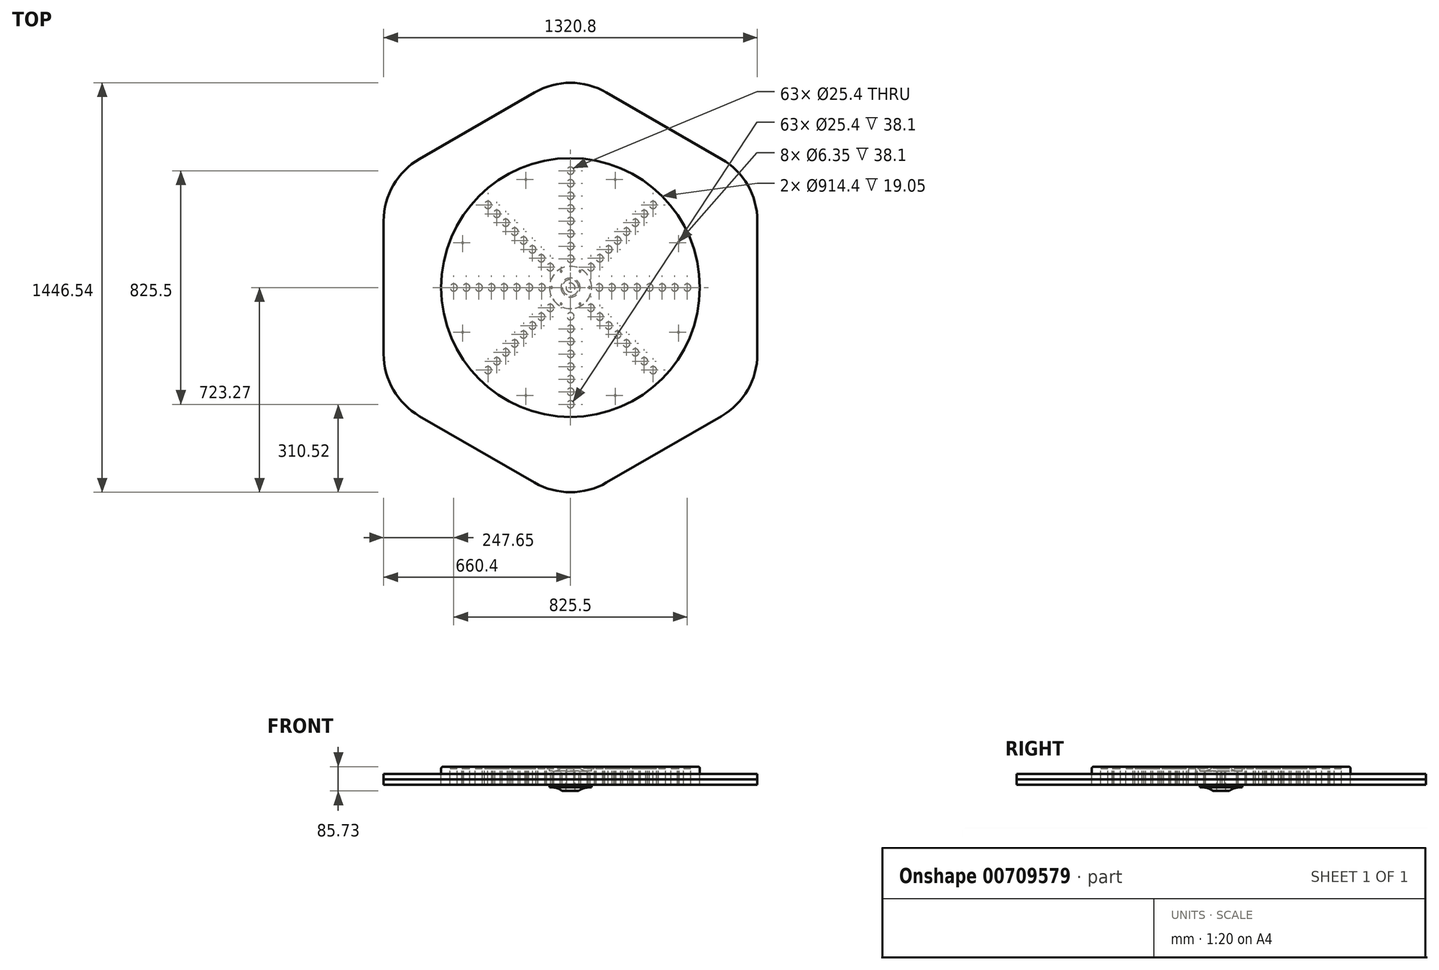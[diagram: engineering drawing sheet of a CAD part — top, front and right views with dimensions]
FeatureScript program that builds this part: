
annotation { "Feature Type Name" : "Feature", "Feature Type Description" : "" }
export const myFeature = defineFeature(function(context is Context, id is Id, definition is map)
    precondition{}
    {
        {
            var Q0;
            Q0=qCreatedBy(makeId("Top.planeOp"),FACE);
            var sketch = newSketch(context, id + "F0", { "sketchPlane" : qUnion([Q0])});
            skCircle(sketch, "E0", {"center": v(0, 0) * mm, "radius": 457.2 * mm});
            skSolve(sketch);
        }
        {
            var Q0;
            Q0=makeQuery(id+"F0.imprint","IMPRINT",FACE,{"disambiguationData":[TD([[makeQuery(id+"F0.imprint","IMPRINT",EDGE,{"derivedFrom":sQuery(id+"F0.wireOp",EDGE,"E0")}),1.0]])]});
            extrude(context, id + "F1", {"entities" : qUnion([Q0]), "oppositeDirection" : true, "depth" : 6.35 * mm, "offsetDistance" : 25.4 * mm});
        }
        {
            var Q0;
            Q0=makeQuery(id+"F1.opExtrude","CAP_FACE",FACE,{"disambiguationData":[OSD([sQuery(id+"F0.wireOp",EDGE,"E0")])],"isStart":false});
            var sketch = newSketch(context, id + "F2", { "sketchPlane" : qUnion([Q0])});
            skCircle(sketch, "E1", {"center": v(0, 0) * mm, "radius": 457.2 * mm});
            skLineSegment(sketch, "E2", {"start": v(0, 0) * mm, "end": v(457.2, 0) * mm, "construction": true});
            skCircle(sketch, "E3", {"center": v(101.6, 0) * mm, "radius": 12.7 * mm});
            skCircle(sketch, "E4.1.0.0", {"center": v(146.05, 0) * mm, "radius": 12.7 * mm});
            skCircle(sketch, "E4.2.0.0", {"center": v(190.5, 0) * mm, "radius": 12.7 * mm});
            skCircle(sketch, "E4.3.0.0", {"center": v(234.95, 0) * mm, "radius": 12.7 * mm});
            skCircle(sketch, "E4.4.0.0", {"center": v(279.4, 0) * mm, "radius": 12.7 * mm});
            skCircle(sketch, "E4.5.0.0", {"center": v(323.85, 0) * mm, "radius": 12.7 * mm});
            skCircle(sketch, "E4.6.0.0", {"center": v(368.3, 0) * mm, "radius": 12.7 * mm});
            skCircle(sketch, "E4.7.0.0", {"center": v(412.75, 0) * mm, "radius": 12.7 * mm});
            skLineSegment(sketch, "E4.direction1", {"start": v(101.6, 0) * mm, "end": v(146.05, 0) * mm, "construction": true});
            skCircle(sketch, "E5.1.0", {"center": v(103.27, 103.27) * mm, "radius": 12.7 * mm});
            skCircle(sketch, "E5.1.1", {"center": v(229, 229) * mm, "radius": 12.7 * mm});
            skCircle(sketch, "E5.1.2", {"center": v(71.84, 71.84) * mm, "radius": 12.7 * mm});
            skCircle(sketch, "E5.1.3", {"center": v(260.43, 260.43) * mm, "radius": 12.7 * mm});
            skCircle(sketch, "E5.1.4", {"center": v(291.86, 291.86) * mm, "radius": 12.7 * mm});
            skCircle(sketch, "E5.1.5", {"center": v(134.7, 134.7) * mm, "radius": 12.7 * mm});
            skCircle(sketch, "E5.1.6", {"center": v(166.13, 166.13) * mm, "radius": 12.7 * mm});
            skLineSegment(sketch, "E5.1.7", {"start": v(71.84, 71.84) * mm, "end": v(103.27, 103.27) * mm, "construction": true});
            skCircle(sketch, "E5.1.8", {"center": v(197.57, 197.57) * mm, "radius": 12.7 * mm});
            skCircle(sketch, "E5.2.0", {"center": v(0, 146.05) * mm, "radius": 12.7 * mm});
            skCircle(sketch, "E5.2.1", {"center": v(0, 323.85) * mm, "radius": 12.7 * mm});
            skCircle(sketch, "E5.2.2", {"center": v(0, 101.6) * mm, "radius": 12.7 * mm});
            skCircle(sketch, "E5.2.3", {"center": v(0, 368.3) * mm, "radius": 12.7 * mm});
            skCircle(sketch, "E5.2.4", {"center": v(0, 412.75) * mm, "radius": 12.7 * mm});
            skCircle(sketch, "E5.2.5", {"center": v(0, 190.5) * mm, "radius": 12.7 * mm});
            skCircle(sketch, "E5.2.6", {"center": v(0, 234.95) * mm, "radius": 12.7 * mm});
            skLineSegment(sketch, "E5.2.7", {"start": v(0, 101.6) * mm, "end": v(0, 146.05) * mm, "construction": true});
            skCircle(sketch, "E5.2.8", {"center": v(0, 279.4) * mm, "radius": 12.7 * mm});
            skCircle(sketch, "E5.3.0", {"center": v(-103.27, 103.27) * mm, "radius": 12.7 * mm});
            skCircle(sketch, "E5.3.1", {"center": v(-229, 229) * mm, "radius": 12.7 * mm});
            skCircle(sketch, "E5.3.2", {"center": v(-71.84, 71.84) * mm, "radius": 12.7 * mm});
            skCircle(sketch, "E5.3.3", {"center": v(-260.43, 260.43) * mm, "radius": 12.7 * mm});
            skCircle(sketch, "E5.3.4", {"center": v(-291.86, 291.86) * mm, "radius": 12.7 * mm});
            skCircle(sketch, "E5.3.5", {"center": v(-134.7, 134.7) * mm, "radius": 12.7 * mm});
            skCircle(sketch, "E5.3.6", {"center": v(-166.13, 166.13) * mm, "radius": 12.7 * mm});
            skLineSegment(sketch, "E5.3.7", {"start": v(-71.84, 71.84) * mm, "end": v(-103.27, 103.27) * mm, "construction": true});
            skCircle(sketch, "E5.3.8", {"center": v(-197.57, 197.57) * mm, "radius": 12.7 * mm});
            skCircle(sketch, "E5.4.0", {"center": v(-146.05, 0) * mm, "radius": 12.7 * mm});
            skCircle(sketch, "E5.4.1", {"center": v(-323.85, 0) * mm, "radius": 12.7 * mm});
            skCircle(sketch, "E5.4.2", {"center": v(-101.6, 0) * mm, "radius": 12.7 * mm});
            skCircle(sketch, "E5.4.3", {"center": v(-368.3, 0) * mm, "radius": 12.7 * mm});
            skCircle(sketch, "E5.4.4", {"center": v(-412.75, 0) * mm, "radius": 12.7 * mm});
            skCircle(sketch, "E5.4.5", {"center": v(-190.5, 0) * mm, "radius": 12.7 * mm});
            skCircle(sketch, "E5.4.6", {"center": v(-234.95, 0) * mm, "radius": 12.7 * mm});
            skLineSegment(sketch, "E5.4.7", {"start": v(-101.6, 0) * mm, "end": v(-146.05, 0) * mm, "construction": true});
            skCircle(sketch, "E5.4.8", {"center": v(-279.4, 0) * mm, "radius": 12.7 * mm});
            skCircle(sketch, "E5.5.0", {"center": v(-103.27, -103.27) * mm, "radius": 12.7 * mm});
            skCircle(sketch, "E5.5.1", {"center": v(-229, -229) * mm, "radius": 12.7 * mm});
            skCircle(sketch, "E5.5.2", {"center": v(-71.84, -71.84) * mm, "radius": 12.7 * mm});
            skCircle(sketch, "E5.5.3", {"center": v(-260.43, -260.43) * mm, "radius": 12.7 * mm});
            skCircle(sketch, "E5.5.4", {"center": v(-291.86, -291.86) * mm, "radius": 12.7 * mm});
            skCircle(sketch, "E5.5.5", {"center": v(-134.7, -134.7) * mm, "radius": 12.7 * mm});
            skCircle(sketch, "E5.5.6", {"center": v(-166.13, -166.13) * mm, "radius": 12.7 * mm});
            skLineSegment(sketch, "E5.5.7", {"start": v(-71.84, -71.84) * mm, "end": v(-103.27, -103.27) * mm, "construction": true});
            skCircle(sketch, "E5.5.8", {"center": v(-197.57, -197.57) * mm, "radius": 12.7 * mm});
            skCircle(sketch, "E5.6.0", {"center": v(0, -146.05) * mm, "radius": 12.7 * mm});
            skCircle(sketch, "E5.6.1", {"center": v(0, -323.85) * mm, "radius": 12.7 * mm});
            skCircle(sketch, "E5.6.2", {"center": v(0, -101.6) * mm, "radius": 12.7 * mm});
            skCircle(sketch, "E5.6.3", {"center": v(0, -368.3) * mm, "radius": 12.7 * mm});
            skCircle(sketch, "E5.6.4", {"center": v(0, -412.75) * mm, "radius": 12.7 * mm});
            skCircle(sketch, "E5.6.5", {"center": v(0, -190.5) * mm, "radius": 12.7 * mm});
            skCircle(sketch, "E5.6.6", {"center": v(0, -234.95) * mm, "radius": 12.7 * mm});
            skLineSegment(sketch, "E5.6.7", {"start": v(0, -101.6) * mm, "end": v(0, -146.05) * mm, "construction": true});
            skCircle(sketch, "E5.6.8", {"center": v(0, -279.4) * mm, "radius": 12.7 * mm});
            skCircle(sketch, "E5.7.0", {"center": v(103.27, -103.27) * mm, "radius": 12.7 * mm});
            skCircle(sketch, "E5.7.1", {"center": v(229, -229) * mm, "radius": 12.7 * mm});
            skCircle(sketch, "E5.7.2", {"center": v(71.84, -71.84) * mm, "radius": 12.7 * mm});
            skCircle(sketch, "E5.7.3", {"center": v(260.43, -260.43) * mm, "radius": 12.7 * mm});
            skCircle(sketch, "E5.7.4", {"center": v(291.86, -291.86) * mm, "radius": 12.7 * mm});
            skCircle(sketch, "E5.7.5", {"center": v(134.7, -134.7) * mm, "radius": 12.7 * mm});
            skCircle(sketch, "E5.7.6", {"center": v(166.13, -166.13) * mm, "radius": 12.7 * mm});
            skLineSegment(sketch, "E5.7.7", {"start": v(71.84, -71.84) * mm, "end": v(103.27, -103.27) * mm, "construction": true});
            skCircle(sketch, "E5.7.8", {"center": v(197.57, -197.57) * mm, "radius": 12.7 * mm});
            skLineSegment(sketch, "E6", {"start": v(0, -412.75) * mm, "end": v(0, 0) * mm, "construction": true});
            skLineSegment(sketch, "E7", {"start": v(0, 0) * mm, "end": v(291.86, -704.6) * mm, "construction": true});
            skCircle(sketch, "E8", {"center": v(0, 0) * mm, "radius": 412.75 * mm, "construction": true});
            skPoint(sketch, "E9", {"position": v(157.95, -381.33) * mm});
            skCircle(sketch, "E10", {"center": v(157.95, -381.33) * mm, "radius": 3.18 * mm});
            skPoint(sketch, "E11.1.0", {"position": v(381.33, -157.95) * mm});
            skPoint(sketch, "E11.2.0", {"position": v(381.33, 157.95) * mm});
            skPoint(sketch, "E11.3.0", {"position": v(157.95, 381.33) * mm});
            skPoint(sketch, "E11.4.0", {"position": v(-157.95, 381.33) * mm});
            skPoint(sketch, "E11.5.0", {"position": v(-381.33, 157.95) * mm});
            skPoint(sketch, "E11.6.0", {"position": v(-381.33, -157.95) * mm});
            skPoint(sketch, "E11.7.0", {"position": v(-157.95, -381.33) * mm});
            skCircle(sketch, "E12", {"center": v(0, 0) * mm, "radius": 74.61 * mm});
            skCircle(sketch, "E13.1.0", {"center": v(381.33, -157.95) * mm, "radius": 3.18 * mm});
            skCircle(sketch, "E13.2.0", {"center": v(381.33, 157.95) * mm, "radius": 3.18 * mm});
            skCircle(sketch, "E13.3.0", {"center": v(157.95, 381.33) * mm, "radius": 3.18 * mm});
            skCircle(sketch, "E13.4.0", {"center": v(-157.95, 381.33) * mm, "radius": 3.18 * mm});
            skCircle(sketch, "E13.5.0", {"center": v(-381.33, 157.95) * mm, "radius": 3.18 * mm});
            skCircle(sketch, "E13.6.0", {"center": v(-381.33, -157.95) * mm, "radius": 3.18 * mm});
            skCircle(sketch, "E13.7.0", {"center": v(-157.95, -381.33) * mm, "radius": 3.18 * mm});
            skSolve(sketch);
        }
        {
            var Q0;
            Q0=makeQuery(id+"F2.imprint","IMPRINT",FACE,{"disambiguationData":[TD([[makeQuery(id+"F2.imprint","IMPRINT",EDGE,{"derivedFrom":sQuery(id+"F2.wireOp",EDGE,"E1")}),-1.0]])]});
            extrude(context, id + "F3", {"entities" : qUnion([Q0]), "depth" : 19.05 * mm, "offsetDistance" : 25.4 * mm});
        }
        {
            var Q0;
            Q0=makeQuery(id+"F3.opExtrude","CAP_FACE",FACE,{"disambiguationData":[OSD([sQuery(id+"F2.wireOp",EDGE,"E1"),sQuery(id+"F2.wireOp",EDGE,"E3"),sQuery(id+"F2.wireOp",EDGE,"E4.1.0.0"),sQuery(id+"F2.wireOp",EDGE,"E4.2.0.0"),sQuery(id+"F2.wireOp",EDGE,"E4.3.0.0"),sQuery(id+"F2.wireOp",EDGE,"E4.4.0.0"),sQuery(id+"F2.wireOp",EDGE,"E4.5.0.0"),sQuery(id+"F2.wireOp",EDGE,"E4.6.0.0"),sQuery(id+"F2.wireOp",EDGE,"E4.7.0.0"),sQuery(id+"F2.wireOp",EDGE,"E5.1.0"),sQuery(id+"F2.wireOp",EDGE,"E5.1.1"),sQuery(id+"F2.wireOp",EDGE,"E5.1.2"),sQuery(id+"F2.wireOp",EDGE,"E5.1.3"),sQuery(id+"F2.wireOp",EDGE,"E5.1.4"),sQuery(id+"F2.wireOp",EDGE,"E5.1.5"),sQuery(id+"F2.wireOp",EDGE,"E5.1.6"),sQuery(id+"F2.wireOp",EDGE,"E5.1.8"),sQuery(id+"F2.wireOp",EDGE,"E5.2.0"),sQuery(id+"F2.wireOp",EDGE,"E5.2.1"),sQuery(id+"F2.wireOp",EDGE,"E5.2.2"),sQuery(id+"F2.wireOp",EDGE,"E5.2.3"),sQuery(id+"F2.wireOp",EDGE,"E5.2.4"),sQuery(id+"F2.wireOp",EDGE,"E5.2.5"),sQuery(id+"F2.wireOp",EDGE,"E5.2.6"),sQuery(id+"F2.wireOp",EDGE,"E5.2.8"),sQuery(id+"F2.wireOp",EDGE,"E5.3.0"),sQuery(id+"F2.wireOp",EDGE,"E5.3.1"),sQuery(id+"F2.wireOp",EDGE,"E5.3.2"),sQuery(id+"F2.wireOp",EDGE,"E5.3.3"),sQuery(id+"F2.wireOp",EDGE,"E5.3.4"),sQuery(id+"F2.wireOp",EDGE,"E5.3.5"),sQuery(id+"F2.wireOp",EDGE,"E5.3.6"),sQuery(id+"F2.wireOp",EDGE,"E5.3.8"),sQuery(id+"F2.wireOp",EDGE,"E5.4.0"),sQuery(id+"F2.wireOp",EDGE,"E5.4.1"),sQuery(id+"F2.wireOp",EDGE,"E5.4.2"),sQuery(id+"F2.wireOp",EDGE,"E5.4.3"),sQuery(id+"F2.wireOp",EDGE,"E5.4.4"),sQuery(id+"F2.wireOp",EDGE,"E5.4.5"),sQuery(id+"F2.wireOp",EDGE,"E5.4.6"),sQuery(id+"F2.wireOp",EDGE,"E5.4.8"),sQuery(id+"F2.wireOp",EDGE,"E5.5.0"),sQuery(id+"F2.wireOp",EDGE,"E5.5.1"),sQuery(id+"F2.wireOp",EDGE,"E5.5.2"),sQuery(id+"F2.wireOp",EDGE,"E5.5.3"),sQuery(id+"F2.wireOp",EDGE,"E5.5.4"),sQuery(id+"F2.wireOp",EDGE,"E5.5.5"),sQuery(id+"F2.wireOp",EDGE,"E5.5.6"),sQuery(id+"F2.wireOp",EDGE,"E5.5.8"),sQuery(id+"F2.wireOp",EDGE,"E5.6.0"),sQuery(id+"F2.wireOp",EDGE,"E5.6.1"),sQuery(id+"F2.wireOp",EDGE,"E5.6.2"),sQuery(id+"F2.wireOp",EDGE,"E5.6.3"),sQuery(id+"F2.wireOp",EDGE,"E5.6.4"),sQuery(id+"F2.wireOp",EDGE,"E5.6.5"),sQuery(id+"F2.wireOp",EDGE,"E5.6.6"),sQuery(id+"F2.wireOp",EDGE,"E5.6.8"),sQuery(id+"F2.wireOp",EDGE,"E5.7.0"),sQuery(id+"F2.wireOp",EDGE,"E5.7.1"),sQuery(id+"F2.wireOp",EDGE,"E5.7.2"),sQuery(id+"F2.wireOp",EDGE,"E5.7.3"),sQuery(id+"F2.wireOp",EDGE,"E5.7.4"),sQuery(id+"F2.wireOp",EDGE,"E5.7.5"),sQuery(id+"F2.wireOp",EDGE,"E5.7.6"),sQuery(id+"F2.wireOp",EDGE,"E5.7.8"),sQuery(id+"F2.wireOp",EDGE,"E10"),sQuery(id+"F2.wireOp",EDGE,"E12"),sQuery(id+"F2.wireOp",EDGE,"E13.1.0"),sQuery(id+"F2.wireOp",EDGE,"E13.2.0"),sQuery(id+"F2.wireOp",EDGE,"E13.3.0"),sQuery(id+"F2.wireOp",EDGE,"E13.4.0"),sQuery(id+"F2.wireOp",EDGE,"E13.5.0"),sQuery(id+"F2.wireOp",EDGE,"E13.6.0"),sQuery(id+"F2.wireOp",EDGE,"E13.7.0")])],"isStart":false});
            var sketch = newSketch(context, id + "F4", { "sketchPlane" : qUnion([Q0])});
            skCircle(sketch, "E14.0", {"center": v(0, 0) * mm, "radius": 457.2 * mm});
            skCircle(sketch, "E14.2", {"center": v(0, 0) * mm, "radius": 457.2 * mm});
            skCircle(sketch, "E15.0", {"center": v(291.86, -291.86) * mm, "radius": 12.7 * mm});
            skCircle(sketch, "E16.0", {"center": v(260.43, -260.43) * mm, "radius": 12.7 * mm});
            skCircle(sketch, "E17.0", {"center": v(229, -229) * mm, "radius": 12.7 * mm});
            skCircle(sketch, "E18.0", {"center": v(197.57, -197.57) * mm, "radius": 12.7 * mm});
            skCircle(sketch, "E19.0", {"center": v(166.13, -166.13) * mm, "radius": 12.7 * mm});
            skCircle(sketch, "E20.0", {"center": v(134.7, -134.7) * mm, "radius": 12.7 * mm});
            skCircle(sketch, "E21.0", {"center": v(103.27, -103.27) * mm, "radius": 12.7 * mm});
            skCircle(sketch, "E22.0", {"center": v(71.84, -71.84) * mm, "radius": 12.7 * mm});
            skCircle(sketch, "E23.0", {"center": v(157.95, -381.33) * mm, "radius": 3.18 * mm});
            skCircle(sketch, "E24.0", {"center": v(381.33, -157.95) * mm, "radius": 3.18 * mm});
            skCircle(sketch, "E25.0", {"center": v(381.33, 157.95) * mm, "radius": 3.18 * mm});
            skCircle(sketch, "E26.0", {"center": v(157.95, 381.33) * mm, "radius": 3.18 * mm});
            skCircle(sketch, "E27.0", {"center": v(-157.95, 381.33) * mm, "radius": 3.18 * mm});
            skCircle(sketch, "E28.0", {"center": v(-381.33, 157.95) * mm, "radius": 3.18 * mm});
            skCircle(sketch, "E29.0", {"center": v(-381.33, -157.95) * mm, "radius": 3.18 * mm});
            skCircle(sketch, "E30.0", {"center": v(101.6, 0) * mm, "radius": 12.7 * mm});
            skCircle(sketch, "E31.0", {"center": v(146.05, 0) * mm, "radius": 12.7 * mm});
            skCircle(sketch, "E32.0", {"center": v(190.5, 0) * mm, "radius": 12.7 * mm});
            skCircle(sketch, "E33.0", {"center": v(234.95, 0) * mm, "radius": 12.7 * mm});
            skCircle(sketch, "E34.0", {"center": v(279.4, 0) * mm, "radius": 12.7 * mm});
            skCircle(sketch, "E35.0", {"center": v(323.85, 0) * mm, "radius": 12.7 * mm});
            skCircle(sketch, "E36.0", {"center": v(368.3, 0) * mm, "radius": 12.7 * mm});
            skCircle(sketch, "E37.0", {"center": v(412.75, 0) * mm, "radius": 12.7 * mm});
            skCircle(sketch, "E38.0", {"center": v(291.86, 291.86) * mm, "radius": 12.7 * mm});
            skCircle(sketch, "E39.0", {"center": v(260.43, 260.43) * mm, "radius": 12.7 * mm});
            skCircle(sketch, "E40.0", {"center": v(229, 229) * mm, "radius": 12.7 * mm});
            skCircle(sketch, "E41.0", {"center": v(197.57, 197.57) * mm, "radius": 12.7 * mm});
            skCircle(sketch, "E42.0", {"center": v(166.13, 166.13) * mm, "radius": 12.7 * mm});
            skCircle(sketch, "E43.0", {"center": v(134.7, 134.7) * mm, "radius": 12.7 * mm});
            skCircle(sketch, "E44.0", {"center": v(103.27, 103.27) * mm, "radius": 12.7 * mm});
            skCircle(sketch, "E45.0", {"center": v(71.84, 71.84) * mm, "radius": 12.7 * mm});
            skCircle(sketch, "E46.0", {"center": v(0, 146.05) * mm, "radius": 12.7 * mm});
            skCircle(sketch, "E47.0", {"center": v(0, 190.5) * mm, "radius": 12.7 * mm});
            skCircle(sketch, "E48.0", {"center": v(0, 234.95) * mm, "radius": 12.7 * mm});
            skCircle(sketch, "E49.0", {"center": v(0, 279.4) * mm, "radius": 12.7 * mm});
            skCircle(sketch, "E50.0", {"center": v(0, 323.85) * mm, "radius": 12.7 * mm});
            skCircle(sketch, "E51.0", {"center": v(0, 368.3) * mm, "radius": 12.7 * mm});
            skCircle(sketch, "E52.0", {"center": v(0, 412.75) * mm, "radius": 12.7 * mm});
            skCircle(sketch, "E53.0", {"center": v(-71.84, 71.84) * mm, "radius": 12.7 * mm});
            skCircle(sketch, "E54.0", {"center": v(-103.27, 103.27) * mm, "radius": 12.7 * mm});
            skCircle(sketch, "E55.0", {"center": v(-134.7, 134.7) * mm, "radius": 12.7 * mm});
            skCircle(sketch, "E56.0", {"center": v(-166.13, 166.13) * mm, "radius": 12.7 * mm});
            skCircle(sketch, "E57.0", {"center": v(-229, 229) * mm, "radius": 12.7 * mm});
            skCircle(sketch, "E58.0", {"center": v(-260.43, 260.43) * mm, "radius": 12.7 * mm});
            skCircle(sketch, "E59.0", {"center": v(-291.86, 291.86) * mm, "radius": 12.7 * mm});
            skCircle(sketch, "E60.0", {"center": v(-101.6, 0) * mm, "radius": 12.7 * mm});
            skCircle(sketch, "E61.0", {"center": v(-190.5, 0) * mm, "radius": 12.7 * mm});
            skCircle(sketch, "E62.0", {"center": v(-234.95, 0) * mm, "radius": 12.7 * mm});
            skCircle(sketch, "E63.0", {"center": v(-197.57, 197.57) * mm, "radius": 12.7 * mm});
            skCircle(sketch, "E64.0", {"center": v(-146.05, 0) * mm, "radius": 12.7 * mm});
            skCircle(sketch, "E65.0", {"center": v(-279.4, 0) * mm, "radius": 12.7 * mm});
            skCircle(sketch, "E66.0", {"center": v(-323.85, 0) * mm, "radius": 12.7 * mm});
            skCircle(sketch, "E67.0", {"center": v(-368.3, 0) * mm, "radius": 12.7 * mm});
            skCircle(sketch, "E68.0", {"center": v(-412.75, 0) * mm, "radius": 12.7 * mm});
            skCircle(sketch, "E69.0", {"center": v(-71.84, -71.84) * mm, "radius": 12.7 * mm});
            skCircle(sketch, "E70.0", {"center": v(-103.27, -103.27) * mm, "radius": 12.7 * mm});
            skCircle(sketch, "E71.0", {"center": v(-134.7, -134.7) * mm, "radius": 12.7 * mm});
            skCircle(sketch, "E72.0", {"center": v(-166.13, -166.13) * mm, "radius": 12.7 * mm});
            skCircle(sketch, "E73.0", {"center": v(-197.57, -197.57) * mm, "radius": 12.7 * mm});
            skCircle(sketch, "E74.0", {"center": v(-229, -229) * mm, "radius": 12.7 * mm});
            skCircle(sketch, "E75.0", {"center": v(-260.43, -260.43) * mm, "radius": 12.7 * mm});
            skCircle(sketch, "E76.0", {"center": v(-291.86, -291.86) * mm, "radius": 12.7 * mm});
            skCircle(sketch, "E77.0", {"center": v(0, -101.6) * mm, "radius": 12.7 * mm});
            skCircle(sketch, "E78.0", {"center": v(0, -146.05) * mm, "radius": 12.7 * mm});
            skCircle(sketch, "E79.0", {"center": v(0, -190.5) * mm, "radius": 12.7 * mm});
            skCircle(sketch, "E80.0", {"center": v(0, -234.95) * mm, "radius": 12.7 * mm});
            skCircle(sketch, "E81.0", {"center": v(0, -279.4) * mm, "radius": 12.7 * mm});
            skCircle(sketch, "E82.0", {"center": v(0, -323.85) * mm, "radius": 12.7 * mm});
            skCircle(sketch, "E83.0", {"center": v(0, -368.3) * mm, "radius": 12.7 * mm});
            skCircle(sketch, "E84.0", {"center": v(0, -412.75) * mm, "radius": 12.7 * mm});
            skCircle(sketch, "E85.0", {"center": v(-157.95, -381.33) * mm, "radius": 3.18 * mm});
            skCircle(sketch, "E86", {"center": v(0, 0) * mm, "radius": 15.88 * mm});
            skCircle(sketch, "E87.cCircle", {"center": v(0, 0) * mm, "radius": 66.68 * mm, "construction": true});
            skLineSegment(sketch, "E87.0", {"start": v(-66.68, 0) * mm, "end": v(-33.34, 57.74) * mm, "construction": true});
            skLineSegment(sketch, "E87.1", {"start": v(-33.34, 57.74) * mm, "end": v(33.34, 57.74) * mm, "construction": true});
            skLineSegment(sketch, "E87.2", {"start": v(33.34, 57.74) * mm, "end": v(66.68, 0) * mm, "construction": true});
            skLineSegment(sketch, "E87.3", {"start": v(66.68, 0) * mm, "end": v(33.34, -57.74) * mm, "construction": true});
            skLineSegment(sketch, "E87.4", {"start": v(33.34, -57.74) * mm, "end": v(-33.34, -57.74) * mm, "construction": true});
            skLineSegment(sketch, "E87.5", {"start": v(-33.34, -57.74) * mm, "end": v(-66.68, 0) * mm, "construction": true});
            skCircle(sketch, "E88", {"center": v(-33.34, -57.74) * mm, "radius": 3.18 * mm});
            skCircle(sketch, "E89.1.0", {"center": v(33.34, -57.74) * mm, "radius": 3.18 * mm});
            skCircle(sketch, "E89.2.0", {"center": v(66.68, 0) * mm, "radius": 3.18 * mm});
            skCircle(sketch, "E89.3.0", {"center": v(33.34, 57.74) * mm, "radius": 3.18 * mm});
            skCircle(sketch, "E89.4.0", {"center": v(-33.34, 57.74) * mm, "radius": 3.18 * mm});
            skCircle(sketch, "E89.5.0", {"center": v(-66.68, 0) * mm, "radius": 3.18 * mm});
            skSolve(sketch);
        }
        {
            var Q0;
            Q0 = qSketchRegion(id + "F4", true);
            extrude(context, id + "F5", {"entities" : qUnion([Q0]), "depth" : 19.05 * mm, "offsetDistance" : 25.4 * mm});
        }
        {
            var Q0;
            Q0=makeQuery(id+"F5.opExtrude","CAP_FACE",FACE,{"disambiguationData":[OSD([sQuery(id+"F4.wireOp",EDGE,"E15.0"),sQuery(id+"F4.wireOp",EDGE,"E16.0"),sQuery(id+"F4.wireOp",EDGE,"E17.0"),sQuery(id+"F4.wireOp",EDGE,"E18.0"),sQuery(id+"F4.wireOp",EDGE,"E19.0"),sQuery(id+"F4.wireOp",EDGE,"E20.0"),sQuery(id+"F4.wireOp",EDGE,"E21.0"),sQuery(id+"F4.wireOp",EDGE,"E22.0"),sQuery(id+"F4.wireOp",EDGE,"E23.0"),sQuery(id+"F4.wireOp",EDGE,"E24.0"),sQuery(id+"F4.wireOp",EDGE,"E25.0"),sQuery(id+"F4.wireOp",EDGE,"E26.0"),sQuery(id+"F4.wireOp",EDGE,"E27.0"),sQuery(id+"F4.wireOp",EDGE,"E28.0"),sQuery(id+"F4.wireOp",EDGE,"E29.0"),sQuery(id+"F4.wireOp",EDGE,"E30.0"),sQuery(id+"F4.wireOp",EDGE,"E31.0"),sQuery(id+"F4.wireOp",EDGE,"E32.0"),sQuery(id+"F4.wireOp",EDGE,"E33.0"),sQuery(id+"F4.wireOp",EDGE,"E34.0"),sQuery(id+"F4.wireOp",EDGE,"E35.0"),sQuery(id+"F4.wireOp",EDGE,"E36.0"),sQuery(id+"F4.wireOp",EDGE,"E37.0"),sQuery(id+"F4.wireOp",EDGE,"E38.0"),sQuery(id+"F4.wireOp",EDGE,"E39.0"),sQuery(id+"F4.wireOp",EDGE,"E40.0"),sQuery(id+"F4.wireOp",EDGE,"E41.0"),sQuery(id+"F4.wireOp",EDGE,"E42.0"),sQuery(id+"F4.wireOp",EDGE,"E43.0"),sQuery(id+"F4.wireOp",EDGE,"E44.0"),sQuery(id+"F4.wireOp",EDGE,"E45.0"),sQuery(id+"F4.wireOp",EDGE,"E46.0"),sQuery(id+"F4.wireOp",EDGE,"E47.0"),sQuery(id+"F4.wireOp",EDGE,"E48.0"),sQuery(id+"F4.wireOp",EDGE,"E49.0"),sQuery(id+"F4.wireOp",EDGE,"E50.0"),sQuery(id+"F4.wireOp",EDGE,"E51.0"),sQuery(id+"F4.wireOp",EDGE,"E52.0"),sQuery(id+"F4.wireOp",EDGE,"E53.0"),sQuery(id+"F4.wireOp",EDGE,"E54.0"),sQuery(id+"F4.wireOp",EDGE,"E55.0"),sQuery(id+"F4.wireOp",EDGE,"E56.0"),sQuery(id+"F4.wireOp",EDGE,"E57.0"),sQuery(id+"F4.wireOp",EDGE,"E58.0"),sQuery(id+"F4.wireOp",EDGE,"E59.0"),sQuery(id+"F4.wireOp",EDGE,"E60.0"),sQuery(id+"F4.wireOp",EDGE,"E61.0"),sQuery(id+"F4.wireOp",EDGE,"E62.0"),sQuery(id+"F4.wireOp",EDGE,"E63.0"),sQuery(id+"F4.wireOp",EDGE,"E64.0"),sQuery(id+"F4.wireOp",EDGE,"E65.0"),sQuery(id+"F4.wireOp",EDGE,"E66.0"),sQuery(id+"F4.wireOp",EDGE,"E67.0"),sQuery(id+"F4.wireOp",EDGE,"E68.0"),sQuery(id+"F4.wireOp",EDGE,"E69.0"),sQuery(id+"F4.wireOp",EDGE,"E70.0"),sQuery(id+"F4.wireOp",EDGE,"E71.0"),sQuery(id+"F4.wireOp",EDGE,"E72.0"),sQuery(id+"F4.wireOp",EDGE,"E73.0"),sQuery(id+"F4.wireOp",EDGE,"E74.0"),sQuery(id+"F4.wireOp",EDGE,"E75.0"),sQuery(id+"F4.wireOp",EDGE,"E76.0"),sQuery(id+"F4.wireOp",EDGE,"E77.0"),sQuery(id+"F4.wireOp",EDGE,"E78.0"),sQuery(id+"F4.wireOp",EDGE,"E79.0"),sQuery(id+"F4.wireOp",EDGE,"E80.0"),sQuery(id+"F4.wireOp",EDGE,"E81.0"),sQuery(id+"F4.wireOp",EDGE,"E82.0"),sQuery(id+"F4.wireOp",EDGE,"E83.0"),sQuery(id+"F4.wireOp",EDGE,"E84.0"),sQuery(id+"F4.wireOp",EDGE,"E85.0"),sQuery(id+"F4.wireOp",EDGE,"E14.0"),sQuery(id+"F4.wireOp",EDGE,"E86"),sQuery(id+"F4.wireOp",EDGE,"E88"),sQuery(id+"F4.wireOp",EDGE,"E89.1.0"),sQuery(id+"F4.wireOp",EDGE,"E89.2.0"),sQuery(id+"F4.wireOp",EDGE,"E89.3.0"),sQuery(id+"F4.wireOp",EDGE,"E89.4.0"),sQuery(id+"F4.wireOp",EDGE,"E89.5.0")])],"isStart":true});
            var sketch = newSketch(context, id + "F6", { "sketchPlane" : qUnion([Q0])});
            skCircle(sketch, "E90.0", {"center": v(66.68, 0) * mm, "radius": 3.18 * mm});
            skCircle(sketch, "E90.1", {"center": v(33.34, 57.74) * mm, "radius": 3.18 * mm});
            skCircle(sketch, "E90.2", {"center": v(-33.34, 57.74) * mm, "radius": 3.18 * mm});
            skCircle(sketch, "E90.3", {"center": v(-66.68, 0) * mm, "radius": 3.18 * mm});
            skCircle(sketch, "E90.4", {"center": v(-33.34, -57.74) * mm, "radius": 3.18 * mm});
            skCircle(sketch, "E90.5", {"center": v(33.34, -57.74) * mm, "radius": 3.18 * mm});
            skCircle(sketch, "E91.0", {"center": v(0, 0) * mm, "radius": 74.61 * mm});
            skCircle(sketch, "E92", {"center": v(0, 0) * mm, "radius": 58.74 * mm});
            skSolve(sketch);
        }
        {
            var Q0;
            Q0=makeQuery(id+"F6.imprint","IMPRINT",FACE,{"disambiguationData":[TD([[makeQuery(id+"F6.imprint","IMPRINT",EDGE,{"derivedFrom":sQuery(id+"F6.wireOp",EDGE,"E90.0")}),1.0]])]});
            extrude(context, id + "F7", {"entities" : qUnion([Q0]), "depth" : 3.17 * mm, "offsetDistance" : 25.4 * mm});
        }
        {
            var Q0;
            Q0=makeQuery(id+"F5.opExtrude","SWEPT_BODY",BODY,{"disambiguationData":[OSD([sQuery(id+"F4.wireOp",EDGE,"E15.0"),sQuery(id+"F4.wireOp",EDGE,"E16.0"),sQuery(id+"F4.wireOp",EDGE,"E17.0"),sQuery(id+"F4.wireOp",EDGE,"E18.0"),sQuery(id+"F4.wireOp",EDGE,"E19.0"),sQuery(id+"F4.wireOp",EDGE,"E20.0"),sQuery(id+"F4.wireOp",EDGE,"E21.0"),sQuery(id+"F4.wireOp",EDGE,"E22.0"),sQuery(id+"F4.wireOp",EDGE,"E23.0"),sQuery(id+"F4.wireOp",EDGE,"E24.0"),sQuery(id+"F4.wireOp",EDGE,"E25.0"),sQuery(id+"F4.wireOp",EDGE,"E26.0"),sQuery(id+"F4.wireOp",EDGE,"E27.0"),sQuery(id+"F4.wireOp",EDGE,"E28.0"),sQuery(id+"F4.wireOp",EDGE,"E29.0"),sQuery(id+"F4.wireOp",EDGE,"E30.0"),sQuery(id+"F4.wireOp",EDGE,"E31.0"),sQuery(id+"F4.wireOp",EDGE,"E32.0"),sQuery(id+"F4.wireOp",EDGE,"E33.0"),sQuery(id+"F4.wireOp",EDGE,"E34.0"),sQuery(id+"F4.wireOp",EDGE,"E35.0"),sQuery(id+"F4.wireOp",EDGE,"E36.0"),sQuery(id+"F4.wireOp",EDGE,"E37.0"),sQuery(id+"F4.wireOp",EDGE,"E38.0"),sQuery(id+"F4.wireOp",EDGE,"E39.0"),sQuery(id+"F4.wireOp",EDGE,"E40.0"),sQuery(id+"F4.wireOp",EDGE,"E41.0"),sQuery(id+"F4.wireOp",EDGE,"E42.0"),sQuery(id+"F4.wireOp",EDGE,"E43.0"),sQuery(id+"F4.wireOp",EDGE,"E44.0"),sQuery(id+"F4.wireOp",EDGE,"E45.0"),sQuery(id+"F4.wireOp",EDGE,"E46.0"),sQuery(id+"F4.wireOp",EDGE,"E47.0"),sQuery(id+"F4.wireOp",EDGE,"E48.0"),sQuery(id+"F4.wireOp",EDGE,"E49.0"),sQuery(id+"F4.wireOp",EDGE,"E50.0"),sQuery(id+"F4.wireOp",EDGE,"E51.0"),sQuery(id+"F4.wireOp",EDGE,"E52.0"),sQuery(id+"F4.wireOp",EDGE,"E53.0"),sQuery(id+"F4.wireOp",EDGE,"E54.0"),sQuery(id+"F4.wireOp",EDGE,"E55.0"),sQuery(id+"F4.wireOp",EDGE,"E56.0"),sQuery(id+"F4.wireOp",EDGE,"E57.0"),sQuery(id+"F4.wireOp",EDGE,"E58.0"),sQuery(id+"F4.wireOp",EDGE,"E59.0"),sQuery(id+"F4.wireOp",EDGE,"E60.0"),sQuery(id+"F4.wireOp",EDGE,"E61.0"),sQuery(id+"F4.wireOp",EDGE,"E62.0"),sQuery(id+"F4.wireOp",EDGE,"E63.0"),sQuery(id+"F4.wireOp",EDGE,"E64.0"),sQuery(id+"F4.wireOp",EDGE,"E65.0"),sQuery(id+"F4.wireOp",EDGE,"E66.0"),sQuery(id+"F4.wireOp",EDGE,"E67.0"),sQuery(id+"F4.wireOp",EDGE,"E68.0"),sQuery(id+"F4.wireOp",EDGE,"E69.0"),sQuery(id+"F4.wireOp",EDGE,"E70.0"),sQuery(id+"F4.wireOp",EDGE,"E71.0"),sQuery(id+"F4.wireOp",EDGE,"E72.0"),sQuery(id+"F4.wireOp",EDGE,"E73.0"),sQuery(id+"F4.wireOp",EDGE,"E74.0"),sQuery(id+"F4.wireOp",EDGE,"E75.0"),sQuery(id+"F4.wireOp",EDGE,"E76.0"),sQuery(id+"F4.wireOp",EDGE,"E77.0"),sQuery(id+"F4.wireOp",EDGE,"E78.0"),sQuery(id+"F4.wireOp",EDGE,"E79.0"),sQuery(id+"F4.wireOp",EDGE,"E80.0"),sQuery(id+"F4.wireOp",EDGE,"E81.0"),sQuery(id+"F4.wireOp",EDGE,"E82.0"),sQuery(id+"F4.wireOp",EDGE,"E83.0"),sQuery(id+"F4.wireOp",EDGE,"E84.0"),sQuery(id+"F4.wireOp",EDGE,"E85.0"),sQuery(id+"F4.wireOp",EDGE,"E14.0"),sQuery(id+"F4.wireOp",EDGE,"E86"),sQuery(id+"F4.wireOp",EDGE,"E88"),sQuery(id+"F4.wireOp",EDGE,"E89.1.0"),sQuery(id+"F4.wireOp",EDGE,"E89.2.0"),sQuery(id+"F4.wireOp",EDGE,"E89.3.0"),sQuery(id+"F4.wireOp",EDGE,"E89.4.0"),sQuery(id+"F4.wireOp",EDGE,"E89.5.0")])]});
            transform(context, id + "F8", {"entities" : qUnion([Q0]), "transformType" : TransformType.TRANSLATION_3D, "dx" : 0 * mm, "dy" : 0 * mm, "dz" : -19.05 * mm, "makeCopy" : true});
        }
        {
            var Q0;
            Q0=makeQuery(id+"F5.opExtrude","CAP_FACE",FACE,{"disambiguationData":[OSD([sQuery(id+"F4.wireOp",EDGE,"E15.0"),sQuery(id+"F4.wireOp",EDGE,"E16.0"),sQuery(id+"F4.wireOp",EDGE,"E17.0"),sQuery(id+"F4.wireOp",EDGE,"E18.0"),sQuery(id+"F4.wireOp",EDGE,"E19.0"),sQuery(id+"F4.wireOp",EDGE,"E20.0"),sQuery(id+"F4.wireOp",EDGE,"E21.0"),sQuery(id+"F4.wireOp",EDGE,"E22.0"),sQuery(id+"F4.wireOp",EDGE,"E23.0"),sQuery(id+"F4.wireOp",EDGE,"E24.0"),sQuery(id+"F4.wireOp",EDGE,"E25.0"),sQuery(id+"F4.wireOp",EDGE,"E26.0"),sQuery(id+"F4.wireOp",EDGE,"E27.0"),sQuery(id+"F4.wireOp",EDGE,"E28.0"),sQuery(id+"F4.wireOp",EDGE,"E29.0"),sQuery(id+"F4.wireOp",EDGE,"E30.0"),sQuery(id+"F4.wireOp",EDGE,"E31.0"),sQuery(id+"F4.wireOp",EDGE,"E32.0"),sQuery(id+"F4.wireOp",EDGE,"E33.0"),sQuery(id+"F4.wireOp",EDGE,"E34.0"),sQuery(id+"F4.wireOp",EDGE,"E35.0"),sQuery(id+"F4.wireOp",EDGE,"E36.0"),sQuery(id+"F4.wireOp",EDGE,"E37.0"),sQuery(id+"F4.wireOp",EDGE,"E38.0"),sQuery(id+"F4.wireOp",EDGE,"E39.0"),sQuery(id+"F4.wireOp",EDGE,"E40.0"),sQuery(id+"F4.wireOp",EDGE,"E41.0"),sQuery(id+"F4.wireOp",EDGE,"E42.0"),sQuery(id+"F4.wireOp",EDGE,"E43.0"),sQuery(id+"F4.wireOp",EDGE,"E44.0"),sQuery(id+"F4.wireOp",EDGE,"E45.0"),sQuery(id+"F4.wireOp",EDGE,"E46.0"),sQuery(id+"F4.wireOp",EDGE,"E47.0"),sQuery(id+"F4.wireOp",EDGE,"E48.0"),sQuery(id+"F4.wireOp",EDGE,"E49.0"),sQuery(id+"F4.wireOp",EDGE,"E50.0"),sQuery(id+"F4.wireOp",EDGE,"E51.0"),sQuery(id+"F4.wireOp",EDGE,"E52.0"),sQuery(id+"F4.wireOp",EDGE,"E53.0"),sQuery(id+"F4.wireOp",EDGE,"E54.0"),sQuery(id+"F4.wireOp",EDGE,"E55.0"),sQuery(id+"F4.wireOp",EDGE,"E56.0"),sQuery(id+"F4.wireOp",EDGE,"E57.0"),sQuery(id+"F4.wireOp",EDGE,"E58.0"),sQuery(id+"F4.wireOp",EDGE,"E59.0"),sQuery(id+"F4.wireOp",EDGE,"E60.0"),sQuery(id+"F4.wireOp",EDGE,"E61.0"),sQuery(id+"F4.wireOp",EDGE,"E62.0"),sQuery(id+"F4.wireOp",EDGE,"E63.0"),sQuery(id+"F4.wireOp",EDGE,"E64.0"),sQuery(id+"F4.wireOp",EDGE,"E65.0"),sQuery(id+"F4.wireOp",EDGE,"E66.0"),sQuery(id+"F4.wireOp",EDGE,"E67.0"),sQuery(id+"F4.wireOp",EDGE,"E68.0"),sQuery(id+"F4.wireOp",EDGE,"E69.0"),sQuery(id+"F4.wireOp",EDGE,"E70.0"),sQuery(id+"F4.wireOp",EDGE,"E71.0"),sQuery(id+"F4.wireOp",EDGE,"E72.0"),sQuery(id+"F4.wireOp",EDGE,"E73.0"),sQuery(id+"F4.wireOp",EDGE,"E74.0"),sQuery(id+"F4.wireOp",EDGE,"E75.0"),sQuery(id+"F4.wireOp",EDGE,"E76.0"),sQuery(id+"F4.wireOp",EDGE,"E77.0"),sQuery(id+"F4.wireOp",EDGE,"E78.0"),sQuery(id+"F4.wireOp",EDGE,"E79.0"),sQuery(id+"F4.wireOp",EDGE,"E80.0"),sQuery(id+"F4.wireOp",EDGE,"E81.0"),sQuery(id+"F4.wireOp",EDGE,"E82.0"),sQuery(id+"F4.wireOp",EDGE,"E83.0"),sQuery(id+"F4.wireOp",EDGE,"E84.0"),sQuery(id+"F4.wireOp",EDGE,"E85.0"),sQuery(id+"F4.wireOp",EDGE,"E14.0"),sQuery(id+"F4.wireOp",EDGE,"E86"),sQuery(id+"F4.wireOp",EDGE,"E88"),sQuery(id+"F4.wireOp",EDGE,"E89.1.0"),sQuery(id+"F4.wireOp",EDGE,"E89.2.0"),sQuery(id+"F4.wireOp",EDGE,"E89.3.0"),sQuery(id+"F4.wireOp",EDGE,"E89.4.0"),sQuery(id+"F4.wireOp",EDGE,"E89.5.0")])],"isStart":true});
            var sketch = newSketch(context, id + "F9", { "sketchPlane" : qUnion([Q0])});
            skCircle(sketch, "E93.cCircle", {"center": v(0, 0) * mm, "radius": 660.4 * mm, "construction": true});
            skLineSegment(sketch, "E93.0", {"start": v(660.4, 234.64) * mm, "end": v(660.4, -234.64) * mm});
            skLineSegment(sketch, "E93.1", {"start": v(533.4, -454.6) * mm, "end": v(127, -689.24) * mm});
            skLineSegment(sketch, "E93.2", {"start": v(-127, -689.24) * mm, "end": v(-533.4, -454.6) * mm});
            skLineSegment(sketch, "E93.3", {"start": v(-660.4, -234.64) * mm, "end": v(-660.4, 234.64) * mm});
            skLineSegment(sketch, "E93.4", {"start": v(-533.4, 454.6) * mm, "end": v(-127, 689.24) * mm});
            skLineSegment(sketch, "E93.5", {"start": v(127, 689.24) * mm, "end": v(533.4, 454.6) * mm});
            skPoint(sketch, "E93.0.midPoint", {"position": v(660.4, 0) * mm});
            skPoint(sketch, "E94.visualSharp", {"position": v(-660.4, 381.28) * mm});
            skArc(sketch, "E94.filletArc", {"start": v(-533.4, 454.6) * mm, "mid": v(-626.37, 361.64) * mm, "end": v(-660.4, 234.64) * mm});
            skPoint(sketch, "E95.visualSharp", {"position": v(0, 762.56) * mm});
            skArc(sketch, "E95.filletArc", {"start": v(127, 689.24) * mm, "mid": v(0, 723.27) * mm, "end": v(-127, 689.24) * mm});
            skPoint(sketch, "E96.visualSharp", {"position": v(660.4, 381.28) * mm});
            skArc(sketch, "E96.filletArc", {"start": v(660.4, 234.64) * mm, "mid": v(626.37, 361.64) * mm, "end": v(533.4, 454.6) * mm});
            skPoint(sketch, "E97.visualSharp", {"position": v(660.4, -381.28) * mm});
            skArc(sketch, "E97.filletArc", {"start": v(533.4, -454.6) * mm, "mid": v(626.37, -361.64) * mm, "end": v(660.4, -234.64) * mm});
            skPoint(sketch, "E98.visualSharp", {"position": v(0, -762.56) * mm});
            skArc(sketch, "E98.filletArc", {"start": v(-127, -689.24) * mm, "mid": v(0, -723.27) * mm, "end": v(127, -689.24) * mm});
            skPoint(sketch, "E99.visualSharp", {"position": v(-660.4, -381.28) * mm});
            skArc(sketch, "E99.filletArc", {"start": v(-660.4, -234.64) * mm, "mid": v(-626.37, -361.64) * mm, "end": v(-533.4, -454.6) * mm});
            skCircle(sketch, "E100.0", {"center": v(0, 0) * mm, "radius": 457.2 * mm});
            skSolve(sketch);
        }
        {
            var Q0;
            Q0 = qSketchRegion(id + "F9", true);
            extrude(context, id + "F10", {"entities" : qUnion([Q0]), "oppositeDirection" : true, "depth" : 19.05 * mm, "offsetDistance" : 25.4 * mm});
        }
        {
            var Q0;
            Q0=makeQuery(id+"F1.opExtrude","CAP_EDGE",EDGE,{"disambiguationData":[OSD([sQuery(id+"F0.wireOp",EDGE,"E0")])],"isStart":true});
            fillet(context, id + "F11", {"entities" : qUnion([Q0]), "radius" : 6.35 * mm, "tangentPropagation" : true, "allowEdgeOverflow" : false});
        }
        {
            var Q0;
            Q0=makeQuery(id+"F10.opExtrude","SWEPT_BODY",BODY,{"disambiguationData":[OSD([sQuery(id+"F9.wireOp",EDGE,"E93.0"),sQuery(id+"F9.wireOp",EDGE,"E93.1"),sQuery(id+"F9.wireOp",EDGE,"E93.2"),sQuery(id+"F9.wireOp",EDGE,"E93.3"),sQuery(id+"F9.wireOp",EDGE,"E93.4"),sQuery(id+"F9.wireOp",EDGE,"E93.5"),sQuery(id+"F9.wireOp",EDGE,"E94.filletArc"),sQuery(id+"F9.wireOp",EDGE,"E95.filletArc"),sQuery(id+"F9.wireOp",EDGE,"E96.filletArc"),sQuery(id+"F9.wireOp",EDGE,"E97.filletArc"),sQuery(id+"F9.wireOp",EDGE,"E98.filletArc"),sQuery(id+"F9.wireOp",EDGE,"E99.filletArc"),sQuery(id+"F9.wireOp",EDGE,"E100.0")])]});
            transform(context, id + "F12", {"entities" : qUnion([Q0]), "transformType" : TransformType.TRANSLATION_3D, "dx" : 0 * mm, "dy" : 0 * mm, "dz" : -19.05 * mm, "makeCopy" : true});
        }
        {
            var Q0;
            Q0=makeQuery(id+"F7.opExtrude","SWEPT_BODY",BODY,{"disambiguationData":[OSD([sQuery(id+"F6.wireOp",EDGE,"E90.0"),sQuery(id+"F6.wireOp",EDGE,"E90.1"),sQuery(id+"F6.wireOp",EDGE,"E90.2"),sQuery(id+"F6.wireOp",EDGE,"E90.3"),sQuery(id+"F6.wireOp",EDGE,"E90.4"),sQuery(id+"F6.wireOp",EDGE,"E90.5"),sQuery(id+"F6.wireOp",EDGE,"E91.0"),sQuery(id+"F6.wireOp",EDGE,"E92")])]});
            transform(context, id + "F13", {"entities" : qUnion([Q0]), "transformType" : TransformType.TRANSLATION_3D, "dx" : 0 * mm, "dy" : 0 * mm, "dz" : -41.27 * mm, "makeCopy" : true});
        }
        {
            var Q0;
            Q0=qCreatedBy(makeId("Front.planeOp"),FACE);
            var sketch = newSketch(context, id + "F14", { "sketchPlane" : qUnion([Q0])});
            skLineSegment(sketch, "E101", {"start": v(0, -22.23) * mm, "end": v(0, 13.17) * mm, "construction": true});
            skLineSegment(sketch, "E102", {"start": v(15.88, -25.4) * mm, "end": v(15.88, -3.18) * mm});
            skLineSegment(sketch, "E103", {"start": v(15.88, -25.4) * mm, "end": v(58.74, -25.4) * mm});
            skLineSegment(sketch, "E104", {"start": v(58.74, -25.4) * mm, "end": v(58.74, -22.23) * mm});
            skLineSegment(sketch, "E105", {"start": v(58.74, -22.23) * mm, "end": v(74.61, -22.23) * mm});
            skLineSegment(sketch, "E106", {"start": v(74.61, -15.88) * mm, "end": v(74.61, -22.23) * mm});
            skLineSegment(sketch, "E107", {"start": v(74.61, -15.88) * mm, "end": v(63.6, -15.88) * mm});
            skLineSegment(sketch, "E108", {"start": v(15.88, -3.18) * mm, "end": v(28.58, -3.18) * mm});
            skLineSegment(sketch, "E109", {"start": v(28.57, -3.17) * mm, "end": v(36.97, -8.34) * mm});
            skPoint(sketch, "E110.visualSharp", {"position": v(49.21, -15.88) * mm});
            skArc(sketch, "E110.filletArc", {"start": v(36.97, -8.34) * mm, "mid": v(49.76, -13.95) * mm, "end": v(63.6, -15.88) * mm});
            skLineSegment(sketch, "E111", {"start": v(58.74, -25.4) * mm, "end": v(15.88, -25.4) * mm});
            skSolve(sketch);
        }
        {
            var Q0;
            Q0=makeQuery(id+"F14.imprint","IMPRINT",FACE,{"disambiguationData":[TD([[makeQuery(id+"F14.imprint","IMPRINT",EDGE,{"derivedFrom":sQuery(id+"F14.wireOp",EDGE,"E102")}),-1.0]])]});
            var Q1;
            Q1=sQuery(id+"F14.wireOp",EDGE,"E101");
            revolve(context, id + "F15", {"surfaceOperationType" : NewSurfaceOperationType.NEW, "entities" : qUnion([Q0]), "axis" : qUnion([Q1]), "revolveType" : RevolveType.FULL});
        }
        {
            var Q0;
            Q0=makeQuery(id+"F15.opRevolve","SWEPT_BODY",BODY,{"disambiguationData":[OSD([sQuery(id+"F14.wireOp",EDGE,"E102"),sQuery(id+"F14.wireOp",EDGE,"E104"),sQuery(id+"F14.wireOp",EDGE,"E106"),sQuery(id+"F14.wireOp",EDGE,"E105"),sQuery(id+"F14.wireOp",EDGE,"E107"),sQuery(id+"F14.wireOp",EDGE,"E108"),sQuery(id+"F14.wireOp",EDGE,"E109"),sQuery(id+"F14.wireOp",EDGE,"E110.filletArc"),sQuery(id+"F14.wireOp",EDGE,"E111")])]});
            var Q1;
            Q1=makeQuery(id+"F5.opExtrude","CAP_FACE",FACE,{"disambiguationData":[OSD([sQuery(id+"F4.wireOp",EDGE,"E15.0"),sQuery(id+"F4.wireOp",EDGE,"E16.0"),sQuery(id+"F4.wireOp",EDGE,"E17.0"),sQuery(id+"F4.wireOp",EDGE,"E18.0"),sQuery(id+"F4.wireOp",EDGE,"E19.0"),sQuery(id+"F4.wireOp",EDGE,"E20.0"),sQuery(id+"F4.wireOp",EDGE,"E21.0"),sQuery(id+"F4.wireOp",EDGE,"E22.0"),sQuery(id+"F4.wireOp",EDGE,"E23.0"),sQuery(id+"F4.wireOp",EDGE,"E24.0"),sQuery(id+"F4.wireOp",EDGE,"E25.0"),sQuery(id+"F4.wireOp",EDGE,"E26.0"),sQuery(id+"F4.wireOp",EDGE,"E27.0"),sQuery(id+"F4.wireOp",EDGE,"E28.0"),sQuery(id+"F4.wireOp",EDGE,"E29.0"),sQuery(id+"F4.wireOp",EDGE,"E30.0"),sQuery(id+"F4.wireOp",EDGE,"E31.0"),sQuery(id+"F4.wireOp",EDGE,"E32.0"),sQuery(id+"F4.wireOp",EDGE,"E33.0"),sQuery(id+"F4.wireOp",EDGE,"E34.0"),sQuery(id+"F4.wireOp",EDGE,"E35.0"),sQuery(id+"F4.wireOp",EDGE,"E36.0"),sQuery(id+"F4.wireOp",EDGE,"E37.0"),sQuery(id+"F4.wireOp",EDGE,"E38.0"),sQuery(id+"F4.wireOp",EDGE,"E39.0"),sQuery(id+"F4.wireOp",EDGE,"E40.0"),sQuery(id+"F4.wireOp",EDGE,"E41.0"),sQuery(id+"F4.wireOp",EDGE,"E42.0"),sQuery(id+"F4.wireOp",EDGE,"E43.0"),sQuery(id+"F4.wireOp",EDGE,"E44.0"),sQuery(id+"F4.wireOp",EDGE,"E45.0"),sQuery(id+"F4.wireOp",EDGE,"E46.0"),sQuery(id+"F4.wireOp",EDGE,"E47.0"),sQuery(id+"F4.wireOp",EDGE,"E48.0"),sQuery(id+"F4.wireOp",EDGE,"E49.0"),sQuery(id+"F4.wireOp",EDGE,"E50.0"),sQuery(id+"F4.wireOp",EDGE,"E51.0"),sQuery(id+"F4.wireOp",EDGE,"E52.0"),sQuery(id+"F4.wireOp",EDGE,"E53.0"),sQuery(id+"F4.wireOp",EDGE,"E54.0"),sQuery(id+"F4.wireOp",EDGE,"E55.0"),sQuery(id+"F4.wireOp",EDGE,"E56.0"),sQuery(id+"F4.wireOp",EDGE,"E57.0"),sQuery(id+"F4.wireOp",EDGE,"E58.0"),sQuery(id+"F4.wireOp",EDGE,"E59.0"),sQuery(id+"F4.wireOp",EDGE,"E60.0"),sQuery(id+"F4.wireOp",EDGE,"E61.0"),sQuery(id+"F4.wireOp",EDGE,"E62.0"),sQuery(id+"F4.wireOp",EDGE,"E63.0"),sQuery(id+"F4.wireOp",EDGE,"E64.0"),sQuery(id+"F4.wireOp",EDGE,"E65.0"),sQuery(id+"F4.wireOp",EDGE,"E66.0"),sQuery(id+"F4.wireOp",EDGE,"E67.0"),sQuery(id+"F4.wireOp",EDGE,"E68.0"),sQuery(id+"F4.wireOp",EDGE,"E69.0"),sQuery(id+"F4.wireOp",EDGE,"E70.0"),sQuery(id+"F4.wireOp",EDGE,"E71.0"),sQuery(id+"F4.wireOp",EDGE,"E72.0"),sQuery(id+"F4.wireOp",EDGE,"E73.0"),sQuery(id+"F4.wireOp",EDGE,"E74.0"),sQuery(id+"F4.wireOp",EDGE,"E75.0"),sQuery(id+"F4.wireOp",EDGE,"E76.0"),sQuery(id+"F4.wireOp",EDGE,"E77.0"),sQuery(id+"F4.wireOp",EDGE,"E78.0"),sQuery(id+"F4.wireOp",EDGE,"E79.0"),sQuery(id+"F4.wireOp",EDGE,"E80.0"),sQuery(id+"F4.wireOp",EDGE,"E81.0"),sQuery(id+"F4.wireOp",EDGE,"E82.0"),sQuery(id+"F4.wireOp",EDGE,"E83.0"),sQuery(id+"F4.wireOp",EDGE,"E84.0"),sQuery(id+"F4.wireOp",EDGE,"E85.0"),sQuery(id+"F4.wireOp",EDGE,"E14.0"),sQuery(id+"F4.wireOp",EDGE,"E86"),sQuery(id+"F4.wireOp",EDGE,"E88"),sQuery(id+"F4.wireOp",EDGE,"E89.1.0"),sQuery(id+"F4.wireOp",EDGE,"E89.2.0"),sQuery(id+"F4.wireOp",EDGE,"E89.3.0"),sQuery(id+"F4.wireOp",EDGE,"E89.4.0"),sQuery(id+"F4.wireOp",EDGE,"E89.5.0")])],"isStart":false});
            mirror(context, id + "F16", {"operationType" : NewBodyOperationType.ADD, "entities" : qUnion([Q0]), "mirrorPlane" : qUnion([Q1])});
        }
    });
